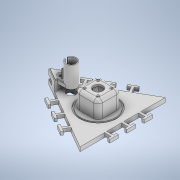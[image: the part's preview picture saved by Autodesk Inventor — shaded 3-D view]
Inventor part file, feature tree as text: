
AUTODESK INVENTOR PART (.ipt)
format: ipt  version: 2022.3 (Build 263350000, 350)  size: 577,024 bytes
history: native  units: mm
features: extrude x21, sketch x14, fillet x7, projected_geometry x2, hole x1
ambient origin geometry x8: Origin, YZ Plane, XZ Plane, XY Plane, X Axis, Y Axis, Z Axis, Center Point
bodies: Solid1 (feature_tree)
feature tree (45):
  sketch  "Sketch1"  dims[d0=200.0mm d1=35.0mm]
  extrude  "Extrusion1"  Depth=35.0mm
  extrude  "Extrusion2"  Depth=5.0mm
  sketch  "Sketch2"  dims[d2=5.0mm d3=5.0mm]
  extrude  "Extrusion3"  Depth=20.0mm
  extrude  "Extrusion4"  Depth=10.0mm TaperAngle=0.0deg
  extrude  "Extrusion5"  Depth=54.0mm
  hole  "Hole1"  [1 undecoded]
  fillet  "Fillet1"  Radius=22.4mm
  fillet  "Fillet2"  [1 undecoded]
  extrude  "Extrusion6"  Depth=35.0mm TaperAngle=0.0deg
  extrude  "Extrusion7"  Depth=31.0mm
  sketch  "Sketch6"  dims[d22=54.0mm d23=5.5mm d24=22.4mm d25=0.0mm d26=0.0mm]
  extrude  "Extrusion8"  Depth=10.0mm
  extrude  "Extrusion9"  Depth=8.0mm
  sketch  "Sketch7"  dims[d27=40.0mm d28=0.0mm d29=35.0mm d30=0.0mm]
  extrude  "Extrusion10"  Depth=2.8mm TaperAngle=0.0deg
  extrude  "Extrusion11"  Depth=3.0mm
  extrude  "Extrusion12"  Depth=1.5mm
  sketch  "Sketch8"  dims[d31=31.0mm d32=31.0mm]
  extrude  "Extrusion13"  Depth=4.0mm
  extrude  "Extrusion14"  Depth=18.0mm
  extrude  "Extrusion15"  Depth=20.0mm TaperAngle=0.0deg
  sketch  "Sketch10"  dims[d41=8.0mm d42=80.0mm]
  extrude  "Extrusion16"  Depth=20.0mm TaperAngle=0.0deg
  extrude  "Extrusion17"  Depth=63.0mm
  extrude  "Extrusion18"  Depth=4.0mm
  fillet  "Fillet3"  Radius=26.0mm
  fillet  "Fillet4"  Radius=8.2mm
  extrude  "Extrusion19"  Depth=4.0mm TaperAngle=0.0deg
  extrude  "Extrusion20"  Depth=15.0mm TaperAngle=0.0deg
  extrude  "Extrusion21"  Depth=20.0mm
  fillet  "Fillet5"  [1 undecoded]
  fillet  "Fillet6"  Radius=22.0mm
  fillet  "Fillet7"  Radius=6.0mm
  sketch  "Sketch3"  dims[d4=20.0mm d5=20.0mm d7=40.0mm d8=20.0mm d10=40.0mm]
  sketch  "Sketch4"  dims[d13=30.0mm d15=360.0deg d17=10.0mm d18=0.0mm]
  sketch  "Sketch5"  dims[d19=2.5mm d20=0.0mm d21=54.0mm]
  sketch  "Sketch9"  dims[d33=3.4mm d34=6.0mm d35=5.9mm d36=2.0mm d37=90.0deg d38=5.0mm d39=0.0mm d40=10.0mm]
  projected_geometry  "Projected Loop1"
  projected_geometry  "Projected Loop2"
  sketch  "Sketch11"  dims[d43=3.5mm d44=2.8mm d45=0.0mm]
  sketch  "Sketch12"  dims[d46=120.0mm d47=3.0mm]
  sketch  "Sketch13"  dims[d48=1.5mm d49=0.0mm d50=31.0mm]
  sketch  "Sketch14"  dims[d51=18.0mm d52=9.0mm d53=18.0mm d54=20.0mm d55=0.0mm d56=20.0mm d57=0.0mm d58=63.0mm d59=19.5mm d61=26.0mm d62=8.2mm d63=24.0mm d64=0.0mm d65=15.0mm d66=0.0mm d67=20.0mm d68=0.0mm d69=0.0mm d70=22.0mm d71=6.0mm d72=6.0mm d73=3.0mm d74=4.0mm d75=2.0mm d76=2.0mm d77=20.0mm d78=0.0mm d79=40.0mm d80=0.0mm d81=1.5mm d82=2.0mm d83=0.0mm d84=2.0mm d85=12.0mm d86=18.0mm d87=0.0mm d88=0.0mm d89=14.5mm d90=0.0mm d91=18.0mm d92=8.0mm d93=0.0mm d94=0.0mm d95=4.0mm d96=2.0mm d97=3.0mm d98=0.0mm d99=18.0mm d100=8.0mm d101=1.0mm d102=2.0mm d103=0.0mm d104=20.0mm d105=5.0mm d106=0.0mm d107=2.0mm d108=4.0mm d109=4.0mm d110=0.0mm d111=0.0mm d112=0.0mm]
note: 3 required parameter values undecoded (feature->parameter linkage not recoverable at this tier; creation-order binding heuristic only, values carry confidence <= 0.55)
